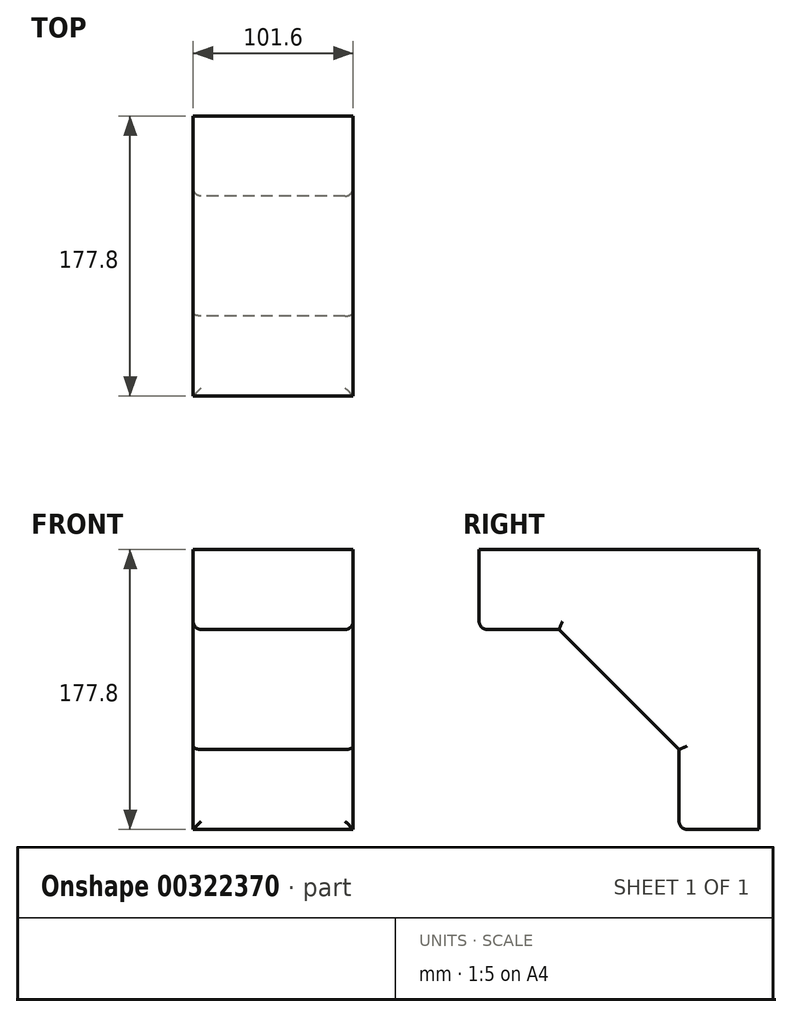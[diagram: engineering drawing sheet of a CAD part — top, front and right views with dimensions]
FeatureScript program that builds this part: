
annotation { "Feature Type Name" : "Feature", "Feature Type Description" : "" }
export const myFeature = defineFeature(function(context is Context, id is Id, definition is map)
    precondition{}
    {
        {
            var Q0;
            Q0=qCreatedBy(makeId("Right.planeOp"),FACE);
            var sketch = newSketch(context, id + "F0", { "sketchPlane" : qUnion([Q0])});
            skLineSegment(sketch, "E0", {"start": v(0, 88.9) * mm, "end": v(-177.8, 88.9) * mm});
            skLineSegment(sketch, "E1", {"start": v(-177.8, 88.9) * mm, "end": v(-177.8, 38.1) * mm});
            skLineSegment(sketch, "E2", {"start": v(-177.8, 38.1) * mm, "end": v(-127, 38.1) * mm});
            skLineSegment(sketch, "E3", {"start": v(-127, 38.1) * mm, "end": v(-50.8, -38.1) * mm});
            skLineSegment(sketch, "E4", {"start": v(-50.8, -38.1) * mm, "end": v(-50.8, -88.9) * mm});
            skLineSegment(sketch, "E5", {"start": v(-50.8, -88.9) * mm, "end": v(0, -88.9) * mm});
            skLineSegment(sketch, "E6", {"start": v(0, -88.9) * mm, "end": v(0, 88.9) * mm});
            skSolve(sketch);
        }
        {
            var Q0;
            Q0=makeQuery(id+"F0.imprint","IMPRINT",FACE,{"disambiguationData":[TD([[makeQuery(id+"F0.imprint","IMPRINT",EDGE,{"derivedFrom":sQuery(id+"F0.wireOp",EDGE,"E0")}),1.0]])]});
            extrude(context, id + "F1", {"entities" : qUnion([Q0]), "endBound" : BoundingType.SYMMETRIC, "depth" : 101.6 * mm});
        }
        {
            var Q0;
            Q0=makeQuery(id+"F1.opExtrude","SWEPT_EDGE",EDGE,{"disambiguationData":[OSD([sQuery(id+"F0.wireOp",EDGE,"E1"),sQuery(id+"F0.wireOp",EDGE,"E2")])]});
            var Q1;
            Q1=makeQuery(id+"F1.opExtrude","CAP_EDGE",EDGE,{"disambiguationData":[OSD([sQuery(id+"F0.wireOp",EDGE,"E2")])],"isStart":false});
            var Q2;
            Q2=makeQuery(id+"F1.opExtrude","CAP_EDGE",EDGE,{"disambiguationData":[OSD([sQuery(id+"F0.wireOp",EDGE,"E3")])],"isStart":false});
            var Q3;
            Q3=makeQuery(id+"F1.opExtrude","CAP_EDGE",EDGE,{"disambiguationData":[OSD([sQuery(id+"F0.wireOp",EDGE,"E4")])],"isStart":false});
            var Q4;
            Q4=makeQuery(id+"F1.opExtrude","SWEPT_EDGE",EDGE,{"disambiguationData":[OSD([sQuery(id+"F0.wireOp",EDGE,"E4"),sQuery(id+"F0.wireOp",EDGE,"E5")])]});
            var Q5;
            Q5=makeQuery(id+"F1.opExtrude","CAP_EDGE",EDGE,{"disambiguationData":[OSD([sQuery(id+"F0.wireOp",EDGE,"E2")])],"isStart":true});
            var Q6;
            Q6=makeQuery(id+"F1.opExtrude","CAP_EDGE",EDGE,{"disambiguationData":[OSD([sQuery(id+"F0.wireOp",EDGE,"E3")])],"isStart":true});
            var Q7;
            Q7=makeQuery(id+"F1.opExtrude","CAP_EDGE",EDGE,{"disambiguationData":[OSD([sQuery(id+"F0.wireOp",EDGE,"E4")])],"isStart":true});
            fillet(context, id + "F2", {"entities" : qUnion([Q0, Q1, Q2, Q3, Q4, Q5, Q6, Q7]), "radius" : 5.08 * mm, "tangentPropagation" : true, "allowEdgeOverflow" : false});
        }
    });
